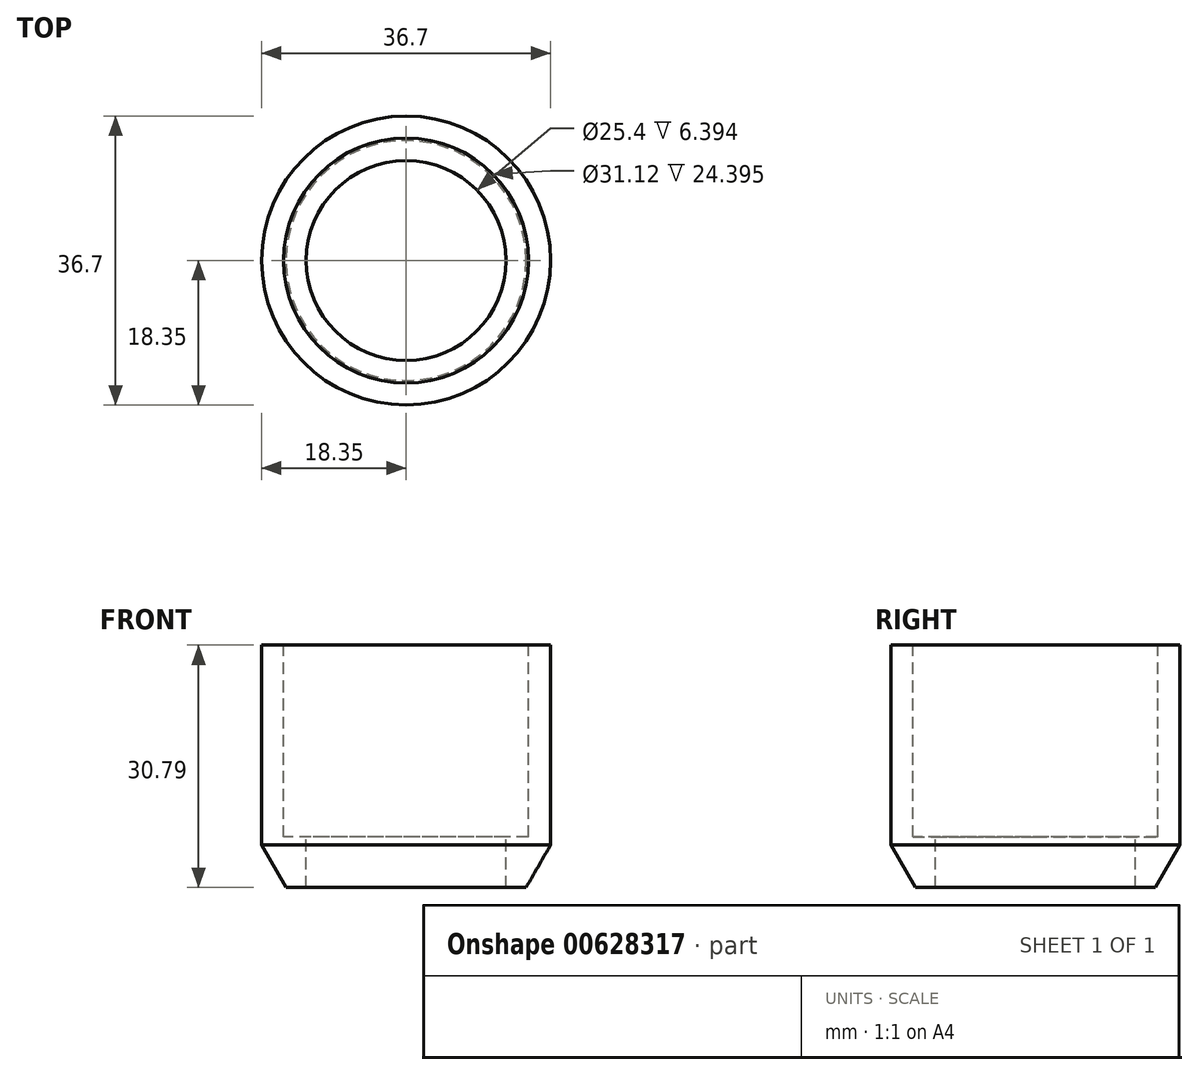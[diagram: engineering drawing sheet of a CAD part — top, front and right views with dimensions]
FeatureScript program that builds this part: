
annotation { "Feature Type Name" : "Feature", "Feature Type Description" : "" }
export const myFeature = defineFeature(function(context is Context, id is Id, definition is map)
    precondition{}
    {
        {
            var Q0;
            Q0=qCreatedBy(makeId("Front.planeOp"),FACE);
            var sketch = newSketch(context, id + "F0", { "sketchPlane" : qUnion([Q0])});
            skLineSegment(sketch, "E0", {"start": v(12.7, -21.8) * mm, "end": v(15.24, -21.8) * mm});
            skLineSegment(sketch, "E1", {"start": v(15.24, -21.8) * mm, "end": v(18.35, -16.4) * mm});
            skLineSegment(sketch, "E2", {"start": v(0, 23.47) * mm, "end": v(0, -26.22) * mm});
            skLineSegment(sketch, "E3", {"start": v(12.7, -21.8) * mm, "end": v(12.7, -15.4) * mm});
            skLineSegment(sketch, "E4", {"start": v(12.7, -15.4) * mm, "end": v(15.56, -15.4) * mm});
            skLineSegment(sketch, "E5", {"start": v(18.35, 9) * mm, "end": v(15.56, 9) * mm});
            skLineSegment(sketch, "E6", {"start": v(15.56, 9) * mm, "end": v(15.56, -15.4) * mm});
            skLineSegment(sketch, "E7", {"start": v(18.35, 9) * mm, "end": v(18.35, -16.4) * mm});
            skSolve(sketch);
        }
        {
            var Q0;
            Q0=makeQuery(id+"F0.imprint","IMPRINT",FACE,{"disambiguationData":[TD([[makeQuery(id+"F0.imprint","IMPRINT",EDGE,{"derivedFrom":sQuery(id+"F0.wireOp",EDGE,"E0")}),1.0]])]});
            var Q1;
            Q1=sQuery(id+"F0.wireOp",EDGE,"E2");
            revolve(context, id + "F1", {"entities" : qUnion([Q0]), "axis" : qUnion([Q1]), "revolveType" : RevolveType.FULL});
        }
    });
